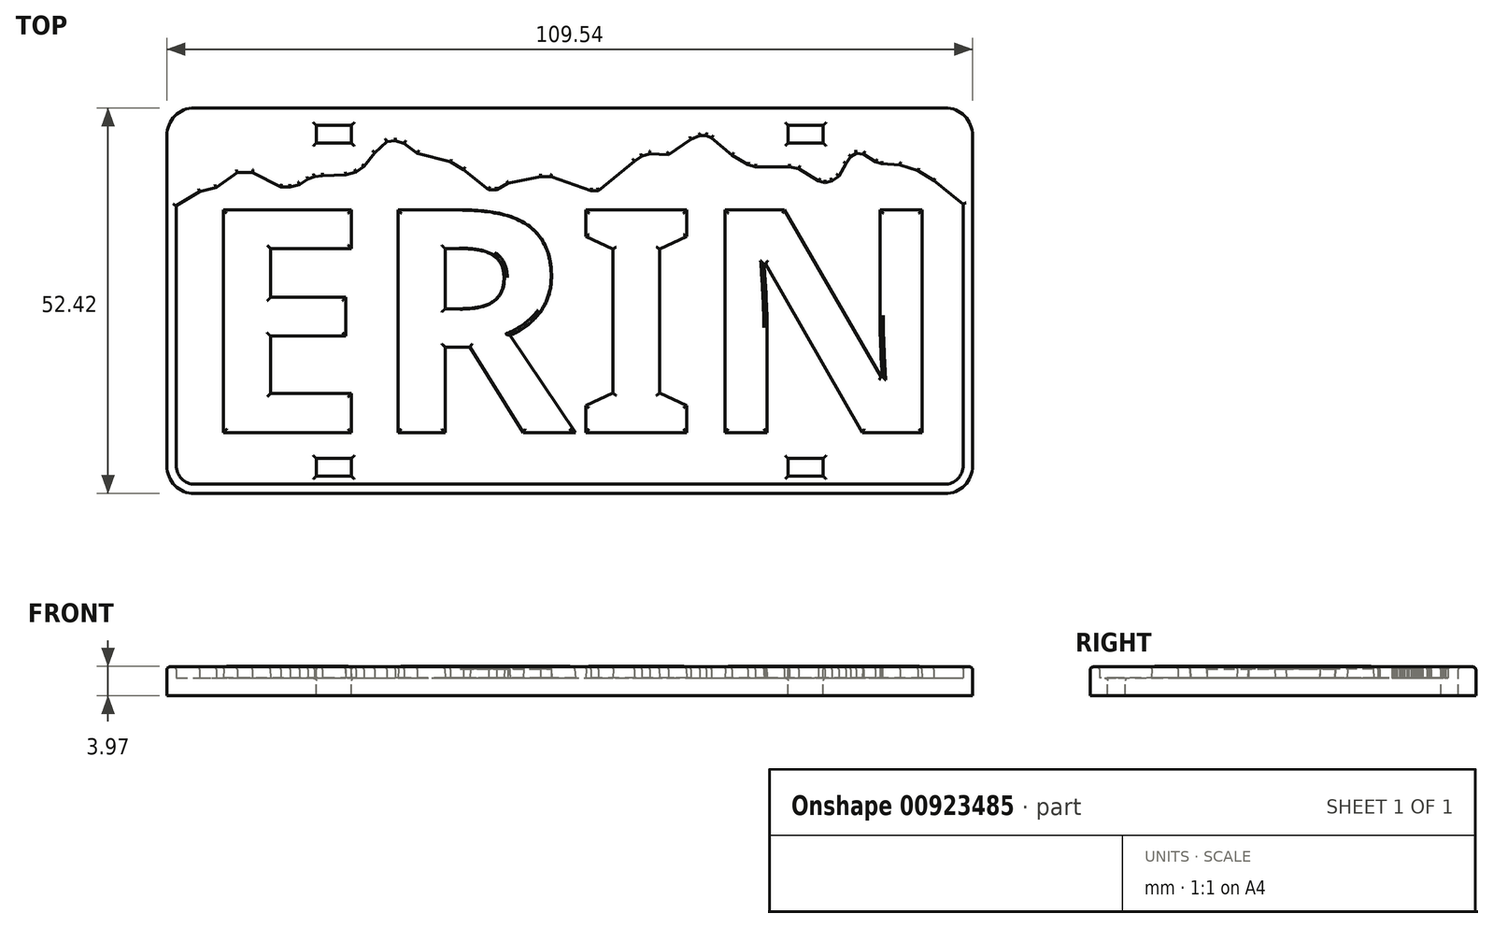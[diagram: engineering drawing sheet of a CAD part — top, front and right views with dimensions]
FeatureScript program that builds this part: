
annotation { "Feature Type Name" : "Feature", "Feature Type Description" : "" }
export const myFeature = defineFeature(function(context is Context, id is Id, definition is map)
    precondition{}
    {
        {
            var Q0;
            Q0=qCreatedBy(makeId("Top.planeOp"),FACE);
            var sketch = newSketch(context, id + "F0", { "sketchPlane" : qUnion([Q0])});
            skLineSegment(sketch, "E0", {"start": v(54.77, -22.46) * mm, "end": v(54.77, 22.46) * mm});
            skArc(sketch, "E1", {"start": v(54.77, 22.46) * mm, "mid": v(53.68, 25.11) * mm, "end": v(51.02, 26.21) * mm});
            skLineSegment(sketch, "E2", {"start": v(51.02, 26.21) * mm, "end": v(-51.02, 26.21) * mm});
            skArc(sketch, "E3", {"start": v(-51.02, 26.21) * mm, "mid": v(-53.68, 25.11) * mm, "end": v(-54.77, 22.46) * mm});
            skLineSegment(sketch, "E4", {"start": v(-54.77, 22.46) * mm, "end": v(-54.77, -22.46) * mm});
            skArc(sketch, "E5", {"start": v(-54.77, -22.46) * mm, "mid": v(-53.54, -25.24) * mm, "end": v(-50.64, -26.2) * mm});
            skLineSegment(sketch, "E6", {"start": v(-50.64, -26.2) * mm, "end": v(51.04, -26.2) * mm});
            skArc(sketch, "E7", {"start": v(51.02, -26.21) * mm, "mid": v(53.68, -25.11) * mm, "end": v(54.77, -22.46) * mm});
            skLineSegment(sketch, "E8", {"start": v(-54.77, 12.13) * mm, "end": v(-50.31, 14.84) * mm});
            skLineSegment(sketch, "E9", {"start": v(-50.31, 14.84) * mm, "end": v(-48.06, 15.4) * mm});
            skLineSegment(sketch, "E10", {"start": v(-48.06, 15.4) * mm, "end": v(-45.2, 17.44) * mm});
            skLineSegment(sketch, "E11", {"start": v(-45.2, 17.44) * mm, "end": v(-43.14, 17.44) * mm});
            skLineSegment(sketch, "E12", {"start": v(-43.14, 17.44) * mm, "end": v(-39.3, 15.5) * mm});
            skLineSegment(sketch, "E13", {"start": v(-39.3, 15.5) * mm, "end": v(-38.03, 15.49) * mm});
            skLineSegment(sketch, "E14", {"start": v(-38.03, 15.49) * mm, "end": v(-36.75, 15.8) * mm});
            skLineSegment(sketch, "E15", {"start": v(-36.75, 15.8) * mm, "end": v(-35.57, 16.54) * mm});
            skLineSegment(sketch, "E16", {"start": v(-35.57, 16.54) * mm, "end": v(-34.73, 16.88) * mm});
            skLineSegment(sketch, "E17", {"start": v(-34.73, 16.88) * mm, "end": v(-33.6, 17.01) * mm});
            skLineSegment(sketch, "E18", {"start": v(-33.6, 17.01) * mm, "end": v(-30.43, 17.11) * mm});
            skLineSegment(sketch, "E19", {"start": v(-29.05, 17.5) * mm, "end": v(-27.98, 18.27) * mm});
            skLineSegment(sketch, "E20", {"start": v(-27.98, 18.27) * mm, "end": v(-26.53, 20.14) * mm});
            skLineSegment(sketch, "E21", {"start": v(-26.53, 20.14) * mm, "end": v(-24.88, 21.63) * mm});
            skLineSegment(sketch, "E22", {"start": v(-24.88, 21.63) * mm, "end": v(-23.73, 21.77) * mm});
            skLineSegment(sketch, "E23", {"start": v(-22.5, 21.4) * mm, "end": v(-20.72, 20.04) * mm});
            skLineSegment(sketch, "E24", {"start": v(-16.23, 18.87) * mm, "end": v(-14.45, 17.85) * mm});
            skLineSegment(sketch, "E25", {"start": v(-14.45, 17.85) * mm, "end": v(-11.02, 15.1) * mm});
            skLineSegment(sketch, "E26", {"start": v(-11.02, 15.1) * mm, "end": v(-9.93, 15.1) * mm});
            skLineSegment(sketch, "E27", {"start": v(-9.93, 15.1) * mm, "end": v(-8.4, 15.96) * mm});
            skLineSegment(sketch, "E28", {"start": v(-8.4, 15.96) * mm, "end": v(-3.94, 16.85) * mm});
            skLineSegment(sketch, "E29", {"start": v(-3.94, 16.85) * mm, "end": v(-2.54, 16.85) * mm});
            skLineSegment(sketch, "E30", {"start": v(-2.54, 16.85) * mm, "end": v(2.9, 14.97) * mm});
            skLineSegment(sketch, "E31", {"start": v(2.9, 14.97) * mm, "end": v(3.92, 14.97) * mm});
            skLineSegment(sketch, "E32", {"start": v(3.92, 14.97) * mm, "end": v(8.8, 18.97) * mm});
            skLineSegment(sketch, "E33", {"start": v(8.8, 18.97) * mm, "end": v(9.82, 19.64) * mm});
            skLineSegment(sketch, "E34", {"start": v(9.82, 19.64) * mm, "end": v(10.9, 19.97) * mm});
            skLineSegment(sketch, "E35", {"start": v(10.9, 19.97) * mm, "end": v(13.43, 19.86) * mm});
            skLineSegment(sketch, "E36", {"start": v(16.5, 21.96) * mm, "end": v(17.71, 22.42) * mm});
            skLineSegment(sketch, "E37", {"start": v(17.71, 22.42) * mm, "end": v(18.56, 22.45) * mm});
            skLineSegment(sketch, "E38", {"start": v(18.56, 22.45) * mm, "end": v(19.28, 22.13) * mm});
            skLineSegment(sketch, "E39", {"start": v(19.28, 22.13) * mm, "end": v(22.05, 19.8) * mm});
            skLineSegment(sketch, "E40", {"start": v(22.05, 19.8) * mm, "end": v(24.2, 18.5) * mm});
            skLineSegment(sketch, "E41", {"start": v(24.2, 18.5) * mm, "end": v(25.23, 18.2) * mm});
            skLineSegment(sketch, "E42", {"start": v(25.23, 18.2) * mm, "end": v(29.85, 18.2) * mm});
            skLineSegment(sketch, "E43", {"start": v(29.85, 18.2) * mm, "end": v(31.13, 17.95) * mm});
            skLineSegment(sketch, "E44", {"start": v(31.13, 17.95) * mm, "end": v(33.84, 16.27) * mm});
            skLineSegment(sketch, "E45", {"start": v(33.84, 16.27) * mm, "end": v(34.73, 16.06) * mm});
            skLineSegment(sketch, "E46", {"start": v(34.73, 16.06) * mm, "end": v(35.67, 16.3) * mm});
            skLineSegment(sketch, "E47", {"start": v(35.67, 16.3) * mm, "end": v(36.58, 16.95) * mm});
            skLineSegment(sketch, "E48", {"start": v(36.58, 16.95) * mm, "end": v(37.58, 18.67) * mm});
            skLineSegment(sketch, "E49", {"start": v(38.22, 19.58) * mm, "end": v(38.96, 20.06) * mm});
            skLineSegment(sketch, "E50", {"start": v(38.96, 20.06) * mm, "end": v(39.94, 19.92) * mm});
            skLineSegment(sketch, "E51", {"start": v(41.58, 18.88) * mm, "end": v(42.4, 18.61) * mm});
            skLineSegment(sketch, "E52", {"start": v(42.4, 18.61) * mm, "end": v(44.9, 18.47) * mm});
            skLineSegment(sketch, "E53", {"start": v(44.9, 18.47) * mm, "end": v(47.31, 17.68) * mm});
            skLineSegment(sketch, "E54", {"start": v(47.31, 17.68) * mm, "end": v(49.47, 16.33) * mm});
            skLineSegment(sketch, "E55", {"start": v(49.47, 16.33) * mm, "end": v(51.88, 14.42) * mm});
            skLineSegment(sketch, "E56", {"start": v(51.88, 14.42) * mm, "end": v(53.78, 12.92) * mm});
            skLineSegment(sketch, "E57", {"start": v(53.78, 12.92) * mm, "end": v(54.77, 12.06) * mm});
            skLineSegment(sketch, "E58", {"start": v(-20.72, 20.04) * mm, "end": v(-16.23, 18.87) * mm});
            skLineSegment(sketch, "E59", {"start": v(16.5, 21.96) * mm, "end": v(13.43, 19.86) * mm});
            skLineSegment(sketch, "E60", {"start": v(-22.5, 21.4) * mm, "end": v(-23.73, 21.77) * mm});
            skLineSegment(sketch, "E61", {"start": v(-29.05, 17.5) * mm, "end": v(-30.43, 17.11) * mm});
            skLineSegment(sketch, "E62", {"start": v(37.58, 18.67) * mm, "end": v(38.22, 19.58) * mm});
            skLineSegment(sketch, "E63", {"start": v(41.58, 18.88) * mm, "end": v(39.94, 19.92) * mm});
            skSolve(sketch);
        }
        {
            var Q0;
            Q0=qCreatedBy(makeId("Top.planeOp"),FACE);
            var sketch = newSketch(context, id + "F1", { "sketchPlane" : qUnion([Q0])});
            skLineSegment(sketch, "E64", {"start": v(54.77, -22.46) * mm, "end": v(54.77, 22.46) * mm});
            skArc(sketch, "E65", {"start": v(54.77, 22.46) * mm, "mid": v(53.68, 25.11) * mm, "end": v(51.02, 26.21) * mm});
            skLineSegment(sketch, "E66", {"start": v(51.02, 26.21) * mm, "end": v(-51.02, 26.21) * mm});
            skArc(sketch, "E67", {"start": v(-51.02, 26.21) * mm, "mid": v(-53.68, 25.11) * mm, "end": v(-54.77, 22.46) * mm});
            skLineSegment(sketch, "E68", {"start": v(-54.77, 22.46) * mm, "end": v(-54.77, -22.46) * mm});
            skArc(sketch, "E69", {"start": v(-54.77, -22.46) * mm, "mid": v(-53.68, -25.11) * mm, "end": v(-51.02, -26.21) * mm});
            skLineSegment(sketch, "E70", {"start": v(-51.02, -26.21) * mm, "end": v(51.02, -26.21) * mm});
            skArc(sketch, "E71", {"start": v(51.02, -26.21) * mm, "mid": v(53.68, -25.11) * mm, "end": v(54.77, -22.46) * mm});
            skLineSegment(sketch, "E72.0", {"start": v(50.96, 24.94) * mm, "end": v(-50.96, 24.94) * mm, "construction": true});
            skLineSegment(sketch, "E72.1", {"start": v(53.5, -22.4) * mm, "end": v(53.5, 22.4) * mm, "construction": true});
            skLineSegment(sketch, "E72.2", {"start": v(-50.96, -24.94) * mm, "end": v(50.96, -24.94) * mm, "construction": true});
            skLineSegment(sketch, "E72.3", {"start": v(-53.5, 22.4) * mm, "end": v(-53.5, -22.4) * mm, "construction": true});
            skPoint(sketch, "E73.visualSharp", {"position": v(-53.5, 24.94) * mm});
            skArc(sketch, "E73.filletArc", {"start": v(-50.96, 24.94) * mm, "mid": v(-52.76, 24.2) * mm, "end": v(-53.5, 22.4) * mm, "construction": true});
            skPoint(sketch, "E74.visualSharp", {"position": v(-53.5, -24.94) * mm});
            skArc(sketch, "E74.filletArc", {"start": v(-53.5, -22.4) * mm, "mid": v(-52.76, -24.2) * mm, "end": v(-50.96, -24.94) * mm, "construction": true});
            skPoint(sketch, "E75.visualSharp", {"position": v(53.5, -24.94) * mm});
            skArc(sketch, "E75.filletArc", {"start": v(50.96, -24.94) * mm, "mid": v(52.76, -24.2) * mm, "end": v(53.5, -22.4) * mm, "construction": true});
            skPoint(sketch, "E76.visualSharp", {"position": v(53.5, 24.94) * mm});
            skArc(sketch, "E76.filletArc", {"start": v(53.5, 22.4) * mm, "mid": v(52.76, 24.2) * mm, "end": v(50.96, 24.94) * mm, "construction": true});
            skSolve(sketch);
        }
        {
            var Q0;
            {var subQ3=sQuery(id+"F0.wireOp",EDGE,"E1");Q0=makeQuery(id+"F0.imprint","IMPRINT",FACE,{"disambiguationData":[TD([[makeQuery(id+"F0.imprint","IMPRINT",EDGE,{"derivedFrom":subQ3}),1.0]])]});}
            extrude(context, id + "F2", {"entities" : qUnion([Q0]), "depth" : 1.52 * mm, "offsetDistance" : 25.4 * mm});
        }
        {
            var Q0;
            Q0=qSketchRegion(id+"F1",true);
            extrude(context, id + "F3", {"entities" : qUnion([Q0]), "operationType" : NewBodyOperationType.ADD, "oppositeDirection" : true, "depth" : 2.38 * mm, "offsetDistance" : 25.4 * mm});
        }
        {
            var Q0;
            {var subQ58=sQuery(id+"F0.wireOp",EDGE,"E0");var subQ59=sQuery(id+"F1.wireOp",EDGE,"E64");var subQ60=sQuery(id+"F1.wireOp",EDGE,"E65");var subQ61=sQuery(id+"F1.wireOp",EDGE,"E68");var subQ62=sQuery(id+"F1.wireOp",EDGE,"E69");var subQ63=sQuery(id+"F1.wireOp",EDGE,"E70");var subQ64=sQuery(id+"F1.wireOp",EDGE,"E71");Q0=makeQuery(id+"F3.boolean.opBoolean","SPLIT",FACE,{"disambiguationData":[TD([makeQuery(id+"F2.opExtrude","SWEPT_FACE",FACE,{"disambiguationData":[OSD([subQ58])]})])],"derivedFrom":makeQuery(id+"F3.opExtrude","CAP_FACE",FACE,{"disambiguationData":[OSD([subQ59,subQ60,sQuery(id+"F1.wireOp",EDGE,"E66"),sQuery(id+"F1.wireOp",EDGE,"E67"),subQ61,subQ62,subQ63,subQ64])],"isStart":true})});}
            var sketch = newSketch(context, id + "F4", { "sketchPlane" : qUnion([Q0])});
            skLineSegment(sketch, "E77", {"start": v(54.77, -22.46) * mm, "end": v(54.77, 12.06) * mm});
            skLineSegment(sketch, "E78", {"start": v(-54.77, 12.13) * mm, "end": v(-54.77, -22.46) * mm});
            skArc(sketch, "E79", {"start": v(-54.77, -22.46) * mm, "mid": v(-53.68, -25.11) * mm, "end": v(-51.02, -26.21) * mm});
            skLineSegment(sketch, "E80", {"start": v(-51.02, -26.21) * mm, "end": v(51.02, -26.21) * mm});
            skArc(sketch, "E81", {"start": v(51.02, -26.21) * mm, "mid": v(53.68, -25.11) * mm, "end": v(54.77, -22.46) * mm});
            skLineSegment(sketch, "E82.1", {"start": v(53.5, -22.4) * mm, "end": v(53.5, 13.14) * mm});
            skLineSegment(sketch, "E82.2", {"start": v(-50.96, -24.94) * mm, "end": v(50.96, -24.94) * mm});
            skLineSegment(sketch, "E82.3", {"start": v(-53.5, 12.9) * mm, "end": v(-53.5, -22.4) * mm});
            skPoint(sketch, "E83.visualSharp", {"position": v(-53.5, 24.94) * mm});
            skPoint(sketch, "E84.visualSharp", {"position": v(-53.5, -24.94) * mm});
            skArc(sketch, "E84.filletArc", {"start": v(-53.5, -22.4) * mm, "mid": v(-52.76, -24.2) * mm, "end": v(-50.96, -24.94) * mm});
            skPoint(sketch, "E85.visualSharp", {"position": v(53.5, -24.94) * mm});
            skArc(sketch, "E85.filletArc", {"start": v(50.96, -24.94) * mm, "mid": v(52.76, -24.2) * mm, "end": v(53.5, -22.4) * mm});
            skPoint(sketch, "E86.visualSharp", {"position": v(53.5, 24.94) * mm});
            skLineSegment(sketch, "E87", {"start": v(-54.77, 12.13) * mm, "end": v(-53.5, 12.9) * mm});
            skLineSegment(sketch, "E88", {"start": v(53.5, 13.14) * mm, "end": v(53.78, 12.92) * mm});
            skLineSegment(sketch, "E89", {"start": v(53.78, 12.92) * mm, "end": v(54.77, 12.06) * mm});
            skSolve(sketch);
        }
        {
            var Q0;
            Q0=qSketchRegion(id+"F4",true);
            extrude(context, id + "F5", {"entities" : qUnion([Q0]), "operationType" : NewBodyOperationType.ADD, "depth" : 1.52 * mm, "offsetDistance" : 25.4 * mm});
        }
        {
            var Q0;
            Q0=makeQuery(id+"F5.boolean.opBoolean","MERGE",FACE,{"derivedFrom":[makeQuery(id+"F2.opExtrude","CAP_FACE",FACE,{"disambiguationData":[OSD([sQuery(id+"F0.wireOp",EDGE,"E0"),sQuery(id+"F0.wireOp",EDGE,"E1"),sQuery(id+"F0.wireOp",EDGE,"E2"),sQuery(id+"F0.wireOp",EDGE,"E3"),sQuery(id+"F0.wireOp",EDGE,"E4"),sQuery(id+"F0.wireOp",EDGE,"E8"),sQuery(id+"F0.wireOp",EDGE,"E9"),sQuery(id+"F0.wireOp",EDGE,"E10"),sQuery(id+"F0.wireOp",EDGE,"E11"),sQuery(id+"F0.wireOp",EDGE,"E12"),sQuery(id+"F0.wireOp",EDGE,"E13"),sQuery(id+"F0.wireOp",EDGE,"E14"),sQuery(id+"F0.wireOp",EDGE,"E15"),sQuery(id+"F0.wireOp",EDGE,"E16"),sQuery(id+"F0.wireOp",EDGE,"E17"),sQuery(id+"F0.wireOp",EDGE,"E18"),sQuery(id+"F0.wireOp",EDGE,"7b9f405e-0691-426e-9c9e-a5372cf0836a"),sQuery(id+"F0.wireOp",EDGE,"E19"),sQuery(id+"F0.wireOp",EDGE,"E20"),sQuery(id+"F0.wireOp",EDGE,"E21"),sQuery(id+"F0.wireOp",EDGE,"E22"),sQuery(id+"F0.wireOp",EDGE,"b3dec5b1-662c-4d50-a13c-af7b7760114a"),sQuery(id+"F0.wireOp",EDGE,"E23"),sQuery(id+"F0.wireOp",EDGE,"4d9ee76e-0833-4cdc-b1a8-2d4ce76e6521"),sQuery(id+"F0.wireOp",EDGE,"E24"),sQuery(id+"F0.wireOp",EDGE,"E25"),sQuery(id+"F0.wireOp",EDGE,"E26"),sQuery(id+"F0.wireOp",EDGE,"E27"),sQuery(id+"F0.wireOp",EDGE,"E28"),sQuery(id+"F0.wireOp",EDGE,"E29"),sQuery(id+"F0.wireOp",EDGE,"E30"),sQuery(id+"F0.wireOp",EDGE,"E31"),sQuery(id+"F0.wireOp",EDGE,"E32"),sQuery(id+"F0.wireOp",EDGE,"E33"),sQuery(id+"F0.wireOp",EDGE,"E34"),sQuery(id+"F0.wireOp",EDGE,"E35"),sQuery(id+"F0.wireOp",EDGE,"55551997-bb9e-4b94-90c5-def3cb147476"),sQuery(id+"F0.wireOp",EDGE,"E36"),sQuery(id+"F0.wireOp",EDGE,"E37"),sQuery(id+"F0.wireOp",EDGE,"E38"),sQuery(id+"F0.wireOp",EDGE,"E39"),sQuery(id+"F0.wireOp",EDGE,"E40"),sQuery(id+"F0.wireOp",EDGE,"E41"),sQuery(id+"F0.wireOp",EDGE,"E42"),sQuery(id+"F0.wireOp",EDGE,"E43"),sQuery(id+"F0.wireOp",EDGE,"E44"),sQuery(id+"F0.wireOp",EDGE,"E45"),sQuery(id+"F0.wireOp",EDGE,"E46"),sQuery(id+"F0.wireOp",EDGE,"E47"),sQuery(id+"F0.wireOp",EDGE,"E48"),sQuery(id+"F0.wireOp",EDGE,"513b7cbe-d979-4e22-b277-f3c42ccdbda1"),sQuery(id+"F0.wireOp",EDGE,"E49"),sQuery(id+"F0.wireOp",EDGE,"E50"),sQuery(id+"F0.wireOp",EDGE,"0d842e13-672c-40e3-aae4-28923e78d4e0"),sQuery(id+"F0.wireOp",EDGE,"E51"),sQuery(id+"F0.wireOp",EDGE,"E52"),sQuery(id+"F0.wireOp",EDGE,"E53"),sQuery(id+"F0.wireOp",EDGE,"E54"),sQuery(id+"F0.wireOp",EDGE,"E55"),sQuery(id+"F0.wireOp",EDGE,"E56"),sQuery(id+"F0.wireOp",EDGE,"E57")])],"isStart":false}),makeQuery(id+"F5.opExtrude","CAP_FACE",FACE,{"disambiguationData":[OSD([sQuery(id+"F4.wireOp",EDGE,"E77"),sQuery(id+"F4.wireOp",EDGE,"E78"),sQuery(id+"F4.wireOp",EDGE,"E79"),sQuery(id+"F4.wireOp",EDGE,"E80"),sQuery(id+"F4.wireOp",EDGE,"E81"),sQuery(id+"F4.wireOp",EDGE,"E82.1"),sQuery(id+"F4.wireOp",EDGE,"E82.2"),sQuery(id+"F4.wireOp",EDGE,"E82.3"),sQuery(id+"F4.wireOp",EDGE,"E84.filletArc"),sQuery(id+"F4.wireOp",EDGE,"E85.filletArc"),sQuery(id+"F4.wireOp",EDGE,"E87"),sQuery(id+"F4.wireOp",EDGE,"E88"),sQuery(id+"F4.wireOp",EDGE,"E89")])],"isStart":false})]});
            var sketch = newSketch(context, id + "F6", { "sketchPlane" : qUnion([Q0])});
            skLineSegment(sketch, "E90.bottom", {"start": v(-34.45, 23.83) * mm, "end": v(-29.7, 23.83) * mm});
            skLineSegment(sketch, "E90.top", {"start": v(-34.45, 21.45) * mm, "end": v(-29.7, 21.45) * mm});
            skLineSegment(sketch, "E90.left", {"start": v(-34.45, 23.83) * mm, "end": v(-34.45, 21.45) * mm});
            skLineSegment(sketch, "E90.right", {"start": v(-29.7, 23.83) * mm, "end": v(-29.7, 21.45) * mm});
            skLineSegment(sketch, "E91", {"start": v(0, 26.21) * mm, "end": v(0, -26.21) * mm, "construction": true});
            skLineSegment(sketch, "E92.MirrorCS", {"start": v(34.45, 23.83) * mm, "end": v(34.45, 21.45) * mm});
            skLineSegment(sketch, "E93.MirrorCS", {"start": v(29.7, 23.83) * mm, "end": v(29.7, 21.45) * mm});
            skLineSegment(sketch, "E94.MirrorCS", {"start": v(34.45, 21.45) * mm, "end": v(29.7, 21.45) * mm});
            skLineSegment(sketch, "E95.MirrorCS", {"start": v(34.45, 23.83) * mm, "end": v(29.7, 23.83) * mm});
            skLineSegment(sketch, "E96", {"start": v(0, 0) * mm, "end": v(-59.23, 0) * mm, "construction": true});
            skLineSegment(sketch, "E97", {"start": v(0, 0) * mm, "end": v(56.47, 0) * mm, "construction": true});
            skLineSegment(sketch, "E98.MirrorCS", {"start": v(-34.45, -23.83) * mm, "end": v(-29.7, -23.83) * mm});
            skLineSegment(sketch, "E99.MirrorCS", {"start": v(-34.45, -23.83) * mm, "end": v(-34.45, -21.45) * mm});
            skLineSegment(sketch, "E100.MirrorCS", {"start": v(-34.45, -21.45) * mm, "end": v(-29.7, -21.45) * mm});
            skLineSegment(sketch, "E101.MirrorCS", {"start": v(-29.7, -23.83) * mm, "end": v(-29.7, -21.45) * mm});
            skLineSegment(sketch, "E102.MirrorCS", {"start": v(29.7, -23.83) * mm, "end": v(29.7, -21.45) * mm});
            skLineSegment(sketch, "E103.MirrorCS", {"start": v(34.45, -23.83) * mm, "end": v(29.7, -23.83) * mm});
            skLineSegment(sketch, "E104.MirrorCS", {"start": v(34.45, -23.83) * mm, "end": v(34.45, -21.45) * mm});
            skLineSegment(sketch, "E105.MirrorCS", {"start": v(34.45, -21.45) * mm, "end": v(29.7, -21.45) * mm});
            skSolve(sketch);
        }
        {
            var Q0;
            Q0=qSketchRegion(id+"F6",true);
            extrude(context, id + "F7", {"entities" : qUnion([Q0]), "operationType" : NewBodyOperationType.REMOVE, "endBound" : BoundingType.THROUGH_ALL, "oppositeDirection" : true, "depth" : 25.4 * mm, "offsetDistance" : 25.4 * mm});
        }
        {
            var Q0;
            Q0=makeQuery(id+"F3.opExtrude","CAP_FACE",FACE,{"disambiguationData":[OSD([sQuery(id+"F1.wireOp",EDGE,"E64"),sQuery(id+"F1.wireOp",EDGE,"E65"),sQuery(id+"F1.wireOp",EDGE,"E66"),sQuery(id+"F1.wireOp",EDGE,"E67"),sQuery(id+"F1.wireOp",EDGE,"E68"),sQuery(id+"F1.wireOp",EDGE,"E69"),sQuery(id+"F1.wireOp",EDGE,"E70"),sQuery(id+"F1.wireOp",EDGE,"E71")])],"isStart":true});
            var sketch = newSketch(context, id + "F8", { "sketchPlane" : qUnion([Q0])});
            skText(sketch, "E106", { "text": "ERIN", "fontName": "NotoSans-Bold.ttf"});
            const initialGuessF8  = {"E106": [-0.0509, -0.0179, 1, 0, 0.03051]};
            skSetInitialGuess(sketch, initialGuessF8);
            skSolve(sketch);
        }
        {
            var Q0;
            Q0=qSketchRegion(id+"F8",true);
            extrude(context, id + "F9", {"entities" : qUnion([Q0]), "operationType" : NewBodyOperationType.ADD, "depth" : 1.59 * mm, "offsetDistance" : 25.4 * mm, "hasDraft" : true, "draftAngle" : 3 * degree, "draftPullDirection" : true});
        }
        {
            var Q0;
            Q0=makeQuery(id+"F5.boolean.opBoolean","MERGE",FACE,{"derivedFrom":[makeQuery(id+"F2.opExtrude","CAP_FACE",FACE,{"disambiguationData":[OSD([sQuery(id+"F0.wireOp",EDGE,"E0"),sQuery(id+"F0.wireOp",EDGE,"E1"),sQuery(id+"F0.wireOp",EDGE,"E2"),sQuery(id+"F0.wireOp",EDGE,"E3"),sQuery(id+"F0.wireOp",EDGE,"E4"),sQuery(id+"F0.wireOp",EDGE,"E8"),sQuery(id+"F0.wireOp",EDGE,"E9"),sQuery(id+"F0.wireOp",EDGE,"E10"),sQuery(id+"F0.wireOp",EDGE,"E11"),sQuery(id+"F0.wireOp",EDGE,"E12"),sQuery(id+"F0.wireOp",EDGE,"E13"),sQuery(id+"F0.wireOp",EDGE,"E14"),sQuery(id+"F0.wireOp",EDGE,"E15"),sQuery(id+"F0.wireOp",EDGE,"E16"),sQuery(id+"F0.wireOp",EDGE,"E17"),sQuery(id+"F0.wireOp",EDGE,"E18"),sQuery(id+"F0.wireOp",EDGE,"7b9f405e-0691-426e-9c9e-a5372cf0836a"),sQuery(id+"F0.wireOp",EDGE,"E19"),sQuery(id+"F0.wireOp",EDGE,"E20"),sQuery(id+"F0.wireOp",EDGE,"E21"),sQuery(id+"F0.wireOp",EDGE,"E22"),sQuery(id+"F0.wireOp",EDGE,"b3dec5b1-662c-4d50-a13c-af7b7760114a"),sQuery(id+"F0.wireOp",EDGE,"E23"),sQuery(id+"F0.wireOp",EDGE,"4d9ee76e-0833-4cdc-b1a8-2d4ce76e6521"),sQuery(id+"F0.wireOp",EDGE,"E24"),sQuery(id+"F0.wireOp",EDGE,"E25"),sQuery(id+"F0.wireOp",EDGE,"E26"),sQuery(id+"F0.wireOp",EDGE,"E27"),sQuery(id+"F0.wireOp",EDGE,"E28"),sQuery(id+"F0.wireOp",EDGE,"E29"),sQuery(id+"F0.wireOp",EDGE,"E30"),sQuery(id+"F0.wireOp",EDGE,"E31"),sQuery(id+"F0.wireOp",EDGE,"E32"),sQuery(id+"F0.wireOp",EDGE,"E33"),sQuery(id+"F0.wireOp",EDGE,"E34"),sQuery(id+"F0.wireOp",EDGE,"E35"),sQuery(id+"F0.wireOp",EDGE,"55551997-bb9e-4b94-90c5-def3cb147476"),sQuery(id+"F0.wireOp",EDGE,"E36"),sQuery(id+"F0.wireOp",EDGE,"E37"),sQuery(id+"F0.wireOp",EDGE,"E38"),sQuery(id+"F0.wireOp",EDGE,"E39"),sQuery(id+"F0.wireOp",EDGE,"E40"),sQuery(id+"F0.wireOp",EDGE,"E41"),sQuery(id+"F0.wireOp",EDGE,"E42"),sQuery(id+"F0.wireOp",EDGE,"E43"),sQuery(id+"F0.wireOp",EDGE,"E44"),sQuery(id+"F0.wireOp",EDGE,"E45"),sQuery(id+"F0.wireOp",EDGE,"E46"),sQuery(id+"F0.wireOp",EDGE,"E47"),sQuery(id+"F0.wireOp",EDGE,"E48"),sQuery(id+"F0.wireOp",EDGE,"513b7cbe-d979-4e22-b277-f3c42ccdbda1"),sQuery(id+"F0.wireOp",EDGE,"E49"),sQuery(id+"F0.wireOp",EDGE,"E50"),sQuery(id+"F0.wireOp",EDGE,"0d842e13-672c-40e3-aae4-28923e78d4e0"),sQuery(id+"F0.wireOp",EDGE,"E51"),sQuery(id+"F0.wireOp",EDGE,"E52"),sQuery(id+"F0.wireOp",EDGE,"E53"),sQuery(id+"F0.wireOp",EDGE,"E54"),sQuery(id+"F0.wireOp",EDGE,"E55"),sQuery(id+"F0.wireOp",EDGE,"E56"),sQuery(id+"F0.wireOp",EDGE,"E57")])],"isStart":false}),makeQuery(id+"F5.opExtrude","CAP_FACE",FACE,{"disambiguationData":[OSD([sQuery(id+"F4.wireOp",EDGE,"E77"),sQuery(id+"F4.wireOp",EDGE,"E78"),sQuery(id+"F4.wireOp",EDGE,"E79"),sQuery(id+"F4.wireOp",EDGE,"E80"),sQuery(id+"F4.wireOp",EDGE,"E81"),sQuery(id+"F4.wireOp",EDGE,"E82.1"),sQuery(id+"F4.wireOp",EDGE,"E82.2"),sQuery(id+"F4.wireOp",EDGE,"E82.3"),sQuery(id+"F4.wireOp",EDGE,"E84.filletArc"),sQuery(id+"F4.wireOp",EDGE,"E85.filletArc"),sQuery(id+"F4.wireOp",EDGE,"E87"),sQuery(id+"F4.wireOp",EDGE,"E88"),sQuery(id+"F4.wireOp",EDGE,"E89")])],"isStart":false})]});
            var Q1;
            {var subQ0=sQuery(id+"F1.wireOp",EDGE,"E64");var subQ1=sQuery(id+"F1.wireOp",EDGE,"E68");var subQ2=sQuery(id+"F1.wireOp",EDGE,"E69");var subQ3=sQuery(id+"F1.wireOp",EDGE,"E70");var subQ4=sQuery(id+"F1.wireOp",EDGE,"E71");Q1=makeQuery(id+"F7.boolean.opBoolean","INTERSECT",EDGE,{"derivedFrom":[makeQuery(id+"F3.boolean.opBoolean","SPLIT",FACE,{"disambiguationData":[TD([makeQuery(id+"F2.opExtrude","SWEPT_FACE",FACE,{"disambiguationData":[OSD([sQuery(id+"F0.wireOp",EDGE,"E0")])]})])],"derivedFrom":makeQuery(id+"F3.opExtrude","CAP_FACE",FACE,{"disambiguationData":[OSD([subQ0,sQuery(id+"F1.wireOp",EDGE,"E65"),sQuery(id+"F1.wireOp",EDGE,"E66"),sQuery(id+"F1.wireOp",EDGE,"E67"),subQ1,subQ2,subQ3,subQ4])],"isStart":true})}),makeQuery(id+"F7.opExtrude","SWEPT_FACE",FACE,{"disambiguationData":[OSD([sQuery(id+"F6.wireOp",EDGE,"E100.MirrorCS")])]})]});}
            var Q2;
            {var subQ0=sQuery(id+"F1.wireOp",EDGE,"E64");var subQ1=sQuery(id+"F1.wireOp",EDGE,"E68");var subQ2=sQuery(id+"F1.wireOp",EDGE,"E69");var subQ3=sQuery(id+"F1.wireOp",EDGE,"E70");var subQ4=sQuery(id+"F1.wireOp",EDGE,"E71");Q2=makeQuery(id+"F7.boolean.opBoolean","INTERSECT",EDGE,{"derivedFrom":[makeQuery(id+"F3.boolean.opBoolean","SPLIT",FACE,{"disambiguationData":[TD([makeQuery(id+"F2.opExtrude","SWEPT_FACE",FACE,{"disambiguationData":[OSD([sQuery(id+"F0.wireOp",EDGE,"E0")])]})])],"derivedFrom":makeQuery(id+"F3.opExtrude","CAP_FACE",FACE,{"disambiguationData":[OSD([subQ0,sQuery(id+"F1.wireOp",EDGE,"E65"),sQuery(id+"F1.wireOp",EDGE,"E66"),sQuery(id+"F1.wireOp",EDGE,"E67"),subQ1,subQ2,subQ3,subQ4])],"isStart":true})}),makeQuery(id+"F7.opExtrude","SWEPT_FACE",FACE,{"disambiguationData":[OSD([sQuery(id+"F6.wireOp",EDGE,"E99.MirrorCS")])]})]});}
            var Q3;
            {var subQ0=sQuery(id+"F1.wireOp",EDGE,"E64");var subQ1=sQuery(id+"F1.wireOp",EDGE,"E68");var subQ2=sQuery(id+"F1.wireOp",EDGE,"E69");var subQ3=sQuery(id+"F1.wireOp",EDGE,"E70");var subQ4=sQuery(id+"F1.wireOp",EDGE,"E71");Q3=makeQuery(id+"F7.boolean.opBoolean","INTERSECT",EDGE,{"derivedFrom":[makeQuery(id+"F3.boolean.opBoolean","SPLIT",FACE,{"disambiguationData":[TD([makeQuery(id+"F2.opExtrude","SWEPT_FACE",FACE,{"disambiguationData":[OSD([sQuery(id+"F0.wireOp",EDGE,"E0")])]})])],"derivedFrom":makeQuery(id+"F3.opExtrude","CAP_FACE",FACE,{"disambiguationData":[OSD([subQ0,sQuery(id+"F1.wireOp",EDGE,"E65"),sQuery(id+"F1.wireOp",EDGE,"E66"),sQuery(id+"F1.wireOp",EDGE,"E67"),subQ1,subQ2,subQ3,subQ4])],"isStart":true})}),makeQuery(id+"F7.opExtrude","SWEPT_FACE",FACE,{"disambiguationData":[OSD([sQuery(id+"F6.wireOp",EDGE,"E98.MirrorCS")])]})]});}
            var Q4;
            {var subQ0=sQuery(id+"F1.wireOp",EDGE,"E64");var subQ1=sQuery(id+"F1.wireOp",EDGE,"E68");var subQ2=sQuery(id+"F1.wireOp",EDGE,"E69");var subQ3=sQuery(id+"F1.wireOp",EDGE,"E70");var subQ4=sQuery(id+"F1.wireOp",EDGE,"E71");Q4=makeQuery(id+"F7.boolean.opBoolean","INTERSECT",EDGE,{"derivedFrom":[makeQuery(id+"F3.boolean.opBoolean","SPLIT",FACE,{"disambiguationData":[TD([makeQuery(id+"F2.opExtrude","SWEPT_FACE",FACE,{"disambiguationData":[OSD([sQuery(id+"F0.wireOp",EDGE,"E0")])]})])],"derivedFrom":makeQuery(id+"F3.opExtrude","CAP_FACE",FACE,{"disambiguationData":[OSD([subQ0,sQuery(id+"F1.wireOp",EDGE,"E65"),sQuery(id+"F1.wireOp",EDGE,"E66"),sQuery(id+"F1.wireOp",EDGE,"E67"),subQ1,subQ2,subQ3,subQ4])],"isStart":true})}),makeQuery(id+"F7.opExtrude","SWEPT_FACE",FACE,{"disambiguationData":[OSD([sQuery(id+"F6.wireOp",EDGE,"E101.MirrorCS")])]})]});}
            var Q5;
            {var subQ0=sQuery(id+"F1.wireOp",EDGE,"E64");var subQ1=sQuery(id+"F1.wireOp",EDGE,"E68");var subQ2=sQuery(id+"F1.wireOp",EDGE,"E69");var subQ3=sQuery(id+"F1.wireOp",EDGE,"E70");var subQ4=sQuery(id+"F1.wireOp",EDGE,"E71");Q5=makeQuery(id+"F7.boolean.opBoolean","INTERSECT",EDGE,{"derivedFrom":[makeQuery(id+"F3.boolean.opBoolean","SPLIT",FACE,{"disambiguationData":[TD([makeQuery(id+"F2.opExtrude","SWEPT_FACE",FACE,{"disambiguationData":[OSD([sQuery(id+"F0.wireOp",EDGE,"E0")])]})])],"derivedFrom":makeQuery(id+"F3.opExtrude","CAP_FACE",FACE,{"disambiguationData":[OSD([subQ0,sQuery(id+"F1.wireOp",EDGE,"E65"),sQuery(id+"F1.wireOp",EDGE,"E66"),sQuery(id+"F1.wireOp",EDGE,"E67"),subQ1,subQ2,subQ3,subQ4])],"isStart":true})}),makeQuery(id+"F7.opExtrude","SWEPT_FACE",FACE,{"disambiguationData":[OSD([sQuery(id+"F6.wireOp",EDGE,"E102.MirrorCS")])]})]});}
            var Q6;
            {var subQ0=sQuery(id+"F1.wireOp",EDGE,"E64");var subQ1=sQuery(id+"F1.wireOp",EDGE,"E68");var subQ2=sQuery(id+"F1.wireOp",EDGE,"E69");var subQ3=sQuery(id+"F1.wireOp",EDGE,"E70");var subQ4=sQuery(id+"F1.wireOp",EDGE,"E71");Q6=makeQuery(id+"F7.boolean.opBoolean","INTERSECT",EDGE,{"derivedFrom":[makeQuery(id+"F3.boolean.opBoolean","SPLIT",FACE,{"disambiguationData":[TD([makeQuery(id+"F2.opExtrude","SWEPT_FACE",FACE,{"disambiguationData":[OSD([sQuery(id+"F0.wireOp",EDGE,"E0")])]})])],"derivedFrom":makeQuery(id+"F3.opExtrude","CAP_FACE",FACE,{"disambiguationData":[OSD([subQ0,sQuery(id+"F1.wireOp",EDGE,"E65"),sQuery(id+"F1.wireOp",EDGE,"E66"),sQuery(id+"F1.wireOp",EDGE,"E67"),subQ1,subQ2,subQ3,subQ4])],"isStart":true})}),makeQuery(id+"F7.opExtrude","SWEPT_FACE",FACE,{"disambiguationData":[OSD([sQuery(id+"F6.wireOp",EDGE,"E105.MirrorCS")])]})]});}
            var Q7;
            {var subQ0=sQuery(id+"F1.wireOp",EDGE,"E64");var subQ1=sQuery(id+"F1.wireOp",EDGE,"E68");var subQ2=sQuery(id+"F1.wireOp",EDGE,"E69");var subQ3=sQuery(id+"F1.wireOp",EDGE,"E70");var subQ4=sQuery(id+"F1.wireOp",EDGE,"E71");Q7=makeQuery(id+"F7.boolean.opBoolean","INTERSECT",EDGE,{"derivedFrom":[makeQuery(id+"F3.boolean.opBoolean","SPLIT",FACE,{"disambiguationData":[TD([makeQuery(id+"F2.opExtrude","SWEPT_FACE",FACE,{"disambiguationData":[OSD([sQuery(id+"F0.wireOp",EDGE,"E0")])]})])],"derivedFrom":makeQuery(id+"F3.opExtrude","CAP_FACE",FACE,{"disambiguationData":[OSD([subQ0,sQuery(id+"F1.wireOp",EDGE,"E65"),sQuery(id+"F1.wireOp",EDGE,"E66"),sQuery(id+"F1.wireOp",EDGE,"E67"),subQ1,subQ2,subQ3,subQ4])],"isStart":true})}),makeQuery(id+"F7.opExtrude","SWEPT_FACE",FACE,{"disambiguationData":[OSD([sQuery(id+"F6.wireOp",EDGE,"E104.MirrorCS")])]})]});}
            var Q8;
            {var subQ0=sQuery(id+"F1.wireOp",EDGE,"E64");var subQ1=sQuery(id+"F1.wireOp",EDGE,"E68");var subQ2=sQuery(id+"F1.wireOp",EDGE,"E69");var subQ3=sQuery(id+"F1.wireOp",EDGE,"E70");var subQ4=sQuery(id+"F1.wireOp",EDGE,"E71");Q8=makeQuery(id+"F7.boolean.opBoolean","INTERSECT",EDGE,{"derivedFrom":[makeQuery(id+"F3.boolean.opBoolean","SPLIT",FACE,{"disambiguationData":[TD([makeQuery(id+"F2.opExtrude","SWEPT_FACE",FACE,{"disambiguationData":[OSD([sQuery(id+"F0.wireOp",EDGE,"E0")])]})])],"derivedFrom":makeQuery(id+"F3.opExtrude","CAP_FACE",FACE,{"disambiguationData":[OSD([subQ0,sQuery(id+"F1.wireOp",EDGE,"E65"),sQuery(id+"F1.wireOp",EDGE,"E66"),sQuery(id+"F1.wireOp",EDGE,"E67"),subQ1,subQ2,subQ3,subQ4])],"isStart":true})}),makeQuery(id+"F7.opExtrude","SWEPT_FACE",FACE,{"disambiguationData":[OSD([sQuery(id+"F6.wireOp",EDGE,"E103.MirrorCS")])]})]});}
            var Q9;
            Q9=makeQuery(id+"F9.opExtrude","CAP_FACE",FACE,{"disambiguationData":[OSD([sQuery(id+"F8.wireOp",EDGE,"E106.sketch_text.stroke-0"),sQuery(id+"F8.wireOp",EDGE,"E106.sketch_text.stroke-1"),sQuery(id+"F8.wireOp",EDGE,"E106.sketch_text.stroke-2"),sQuery(id+"F8.wireOp",EDGE,"E106.sketch_text.stroke-3"),sQuery(id+"F8.wireOp",EDGE,"E106.sketch_text.stroke-4"),sQuery(id+"F8.wireOp",EDGE,"E106.sketch_text.stroke-5"),sQuery(id+"F8.wireOp",EDGE,"E106.sketch_text.stroke-6"),sQuery(id+"F8.wireOp",EDGE,"E106.sketch_text.stroke-7"),sQuery(id+"F8.wireOp",EDGE,"E106.sketch_text.stroke-8"),sQuery(id+"F8.wireOp",EDGE,"E106.sketch_text.stroke-9"),sQuery(id+"F8.wireOp",EDGE,"E106.sketch_text.stroke-10"),sQuery(id+"F8.wireOp",EDGE,"E106.sketch_text.stroke-11"),sQuery(id+"F8.wireOp",EDGE,"E106.sketch_text.stroke-12"),sQuery(id+"F8.wireOp",EDGE,"E106.sketch_text.stroke-13"),sQuery(id+"F8.wireOp",EDGE,"E106.sketch_text.stroke-14")])],"isStart":false});
            var Q10;
            Q10=makeQuery(id+"F9.opExtrude","CAP_FACE",FACE,{"disambiguationData":[OSD([sQuery(id+"F8.wireOp",EDGE,"E106.sketch_text.stroke-15"),sQuery(id+"F8.wireOp",EDGE,"E106.sketch_text.stroke-16"),sQuery(id+"F8.wireOp",EDGE,"E106.sketch_text.stroke-17"),sQuery(id+"F8.wireOp",EDGE,"E106.sketch_text.stroke-18"),sQuery(id+"F8.wireOp",EDGE,"E106.sketch_text.stroke-19"),sQuery(id+"F8.wireOp",EDGE,"E106.sketch_text.stroke-20"),sQuery(id+"F8.wireOp",EDGE,"E106.sketch_text.stroke-21"),sQuery(id+"F8.wireOp",EDGE,"E106.sketch_text.stroke-22"),sQuery(id+"F8.wireOp",EDGE,"E106.sketch_text.stroke-23"),sQuery(id+"F8.wireOp",EDGE,"E106.sketch_text.stroke-24"),sQuery(id+"F8.wireOp",EDGE,"E106.sketch_text.stroke-25"),sQuery(id+"F8.wireOp",EDGE,"E106.sketch_text.stroke-26"),sQuery(id+"F8.wireOp",EDGE,"E106.sketch_text.stroke-27"),sQuery(id+"F8.wireOp",EDGE,"E106.sketch_text.stroke-28")])],"isStart":false});
            var Q11;
            Q11=makeQuery(id+"F9.opExtrude","CAP_FACE",FACE,{"disambiguationData":[OSD([sQuery(id+"F8.wireOp",EDGE,"E106.sketch_text.stroke-29"),sQuery(id+"F8.wireOp",EDGE,"E106.sketch_text.stroke-30"),sQuery(id+"F8.wireOp",EDGE,"E106.sketch_text.stroke-31"),sQuery(id+"F8.wireOp",EDGE,"E106.sketch_text.stroke-32"),sQuery(id+"F8.wireOp",EDGE,"E106.sketch_text.stroke-33"),sQuery(id+"F8.wireOp",EDGE,"E106.sketch_text.stroke-34"),sQuery(id+"F8.wireOp",EDGE,"E106.sketch_text.stroke-35"),sQuery(id+"F8.wireOp",EDGE,"E106.sketch_text.stroke-36"),sQuery(id+"F8.wireOp",EDGE,"E106.sketch_text.stroke-37"),sQuery(id+"F8.wireOp",EDGE,"E106.sketch_text.stroke-38"),sQuery(id+"F8.wireOp",EDGE,"E106.sketch_text.stroke-39"),sQuery(id+"F8.wireOp",EDGE,"E106.sketch_text.stroke-40"),sQuery(id+"F8.wireOp",EDGE,"E106.sketch_text.stroke-41"),sQuery(id+"F8.wireOp",EDGE,"E106.sketch_text.stroke-42")])],"isStart":false});
            var Q12;
            Q12=makeQuery(id+"F9.opExtrude","CAP_FACE",FACE,{"disambiguationData":[OSD([sQuery(id+"F8.wireOp",EDGE,"E106.sketch_text.stroke-57"),sQuery(id+"F8.wireOp",EDGE,"E106.sketch_text.stroke-58"),sQuery(id+"F8.wireOp",EDGE,"E106.sketch_text.stroke-59"),sQuery(id+"F8.wireOp",EDGE,"E106.sketch_text.stroke-60"),sQuery(id+"F8.wireOp",EDGE,"E106.sketch_text.stroke-61"),sQuery(id+"F8.wireOp",EDGE,"E106.sketch_text.stroke-62"),sQuery(id+"F8.wireOp",EDGE,"E106.sketch_text.stroke-63"),sQuery(id+"F8.wireOp",EDGE,"E106.sketch_text.stroke-64"),sQuery(id+"F8.wireOp",EDGE,"E106.sketch_text.stroke-65"),sQuery(id+"F8.wireOp",EDGE,"E106.sketch_text.stroke-66"),sQuery(id+"F8.wireOp",EDGE,"E106.sketch_text.stroke-67"),sQuery(id+"F8.wireOp",EDGE,"E106.sketch_text.stroke-68"),sQuery(id+"F8.wireOp",EDGE,"E106.sketch_text.stroke-69"),sQuery(id+"F8.wireOp",EDGE,"E106.sketch_text.stroke-70")])],"isStart":false});
            var Q13;
            Q13=makeQuery(id+"F9.opExtrude","CAP_FACE",FACE,{"disambiguationData":[OSD([sQuery(id+"F8.wireOp",EDGE,"E106.sketch_text.stroke-71"),sQuery(id+"F8.wireOp",EDGE,"E106.sketch_text.stroke-72"),sQuery(id+"F8.wireOp",EDGE,"E106.sketch_text.stroke-73"),sQuery(id+"F8.wireOp",EDGE,"E106.sketch_text.stroke-74"),sQuery(id+"F8.wireOp",EDGE,"E106.sketch_text.stroke-75"),sQuery(id+"F8.wireOp",EDGE,"E106.sketch_text.stroke-76"),sQuery(id+"F8.wireOp",EDGE,"E106.sketch_text.stroke-77"),sQuery(id+"F8.wireOp",EDGE,"E106.sketch_text.stroke-78"),sQuery(id+"F8.wireOp",EDGE,"E106.sketch_text.stroke-79"),sQuery(id+"F8.wireOp",EDGE,"E106.sketch_text.stroke-80"),sQuery(id+"F8.wireOp",EDGE,"E106.sketch_text.stroke-81"),sQuery(id+"F8.wireOp",EDGE,"E106.sketch_text.stroke-82"),sQuery(id+"F8.wireOp",EDGE,"E106.sketch_text.stroke-83"),sQuery(id+"F8.wireOp",EDGE,"E106.sketch_text.stroke-84"),sQuery(id+"F8.wireOp",EDGE,"E106.sketch_text.stroke-85"),sQuery(id+"F8.wireOp",EDGE,"E106.sketch_text.stroke-86"),sQuery(id+"F8.wireOp",EDGE,"E106.sketch_text.stroke-87"),sQuery(id+"F8.wireOp",EDGE,"E106.sketch_text.stroke-88"),sQuery(id+"F8.wireOp",EDGE,"E106.sketch_text.stroke-89")])],"isStart":false});
            var Q14;
            Q14=makeQuery(id+"F9.opExtrude","CAP_FACE",FACE,{"disambiguationData":[OSD([sQuery(id+"F8.wireOp",EDGE,"E106.sketch_text.stroke-43"),sQuery(id+"F8.wireOp",EDGE,"E106.sketch_text.stroke-44"),sQuery(id+"F8.wireOp",EDGE,"E106.sketch_text.stroke-45"),sQuery(id+"F8.wireOp",EDGE,"E106.sketch_text.stroke-46"),sQuery(id+"F8.wireOp",EDGE,"E106.sketch_text.stroke-47"),sQuery(id+"F8.wireOp",EDGE,"E106.sketch_text.stroke-48"),sQuery(id+"F8.wireOp",EDGE,"E106.sketch_text.stroke-49"),sQuery(id+"F8.wireOp",EDGE,"E106.sketch_text.stroke-50"),sQuery(id+"F8.wireOp",EDGE,"E106.sketch_text.stroke-51"),sQuery(id+"F8.wireOp",EDGE,"E106.sketch_text.stroke-52"),sQuery(id+"F8.wireOp",EDGE,"E106.sketch_text.stroke-53"),sQuery(id+"F8.wireOp",EDGE,"E106.sketch_text.stroke-54"),sQuery(id+"F8.wireOp",EDGE,"E106.sketch_text.stroke-55"),sQuery(id+"F8.wireOp",EDGE,"E106.sketch_text.stroke-56")])],"isStart":false});
            fillet(context, id + "F10", {"entities" : qUnion([Q0, Q1, Q2, Q3, Q4, Q5, Q6, Q7, Q8, Q9, Q10, Q11, Q12, Q13, Q14]), "radius" : 0.38 * mm, "tangentPropagation" : true, "allowEdgeOverflow" : false});
        }
    });
